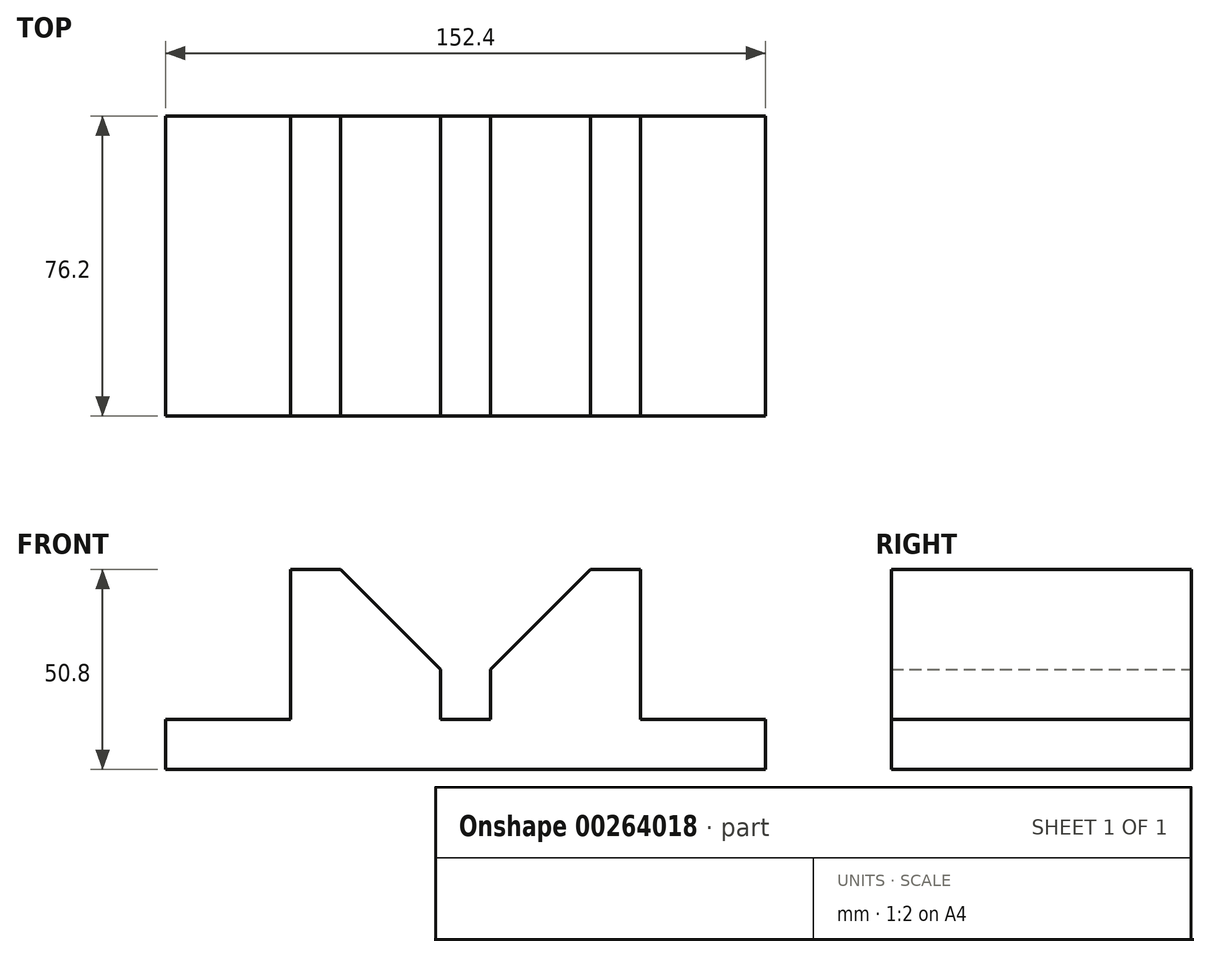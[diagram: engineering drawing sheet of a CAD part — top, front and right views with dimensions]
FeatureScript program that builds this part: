
annotation { "Feature Type Name" : "Feature", "Feature Type Description" : "" }
export const myFeature = defineFeature(function(context is Context, id is Id, definition is map)
    precondition{}
    {
        {
            var Q0;
            Q0=qCreatedBy(makeId("Front.planeOp"),FACE);
            var sketch = newSketch(context, id + "F0", { "sketchPlane" : qUnion([Q0])});
            skLineSegment(sketch, "E0", {"start": v(-76.2, 0) * mm, "end": v(76.2, 0) * mm});
            skLineSegment(sketch, "E1", {"start": v(76.2, 0) * mm, "end": v(76.2, 12.7) * mm});
            skLineSegment(sketch, "E2", {"start": v(76.2, 12.7) * mm, "end": v(44.45, 12.7) * mm});
            skLineSegment(sketch, "E3", {"start": v(44.45, 12.7) * mm, "end": v(44.45, 50.8) * mm});
            skLineSegment(sketch, "E4", {"start": v(44.45, 50.8) * mm, "end": v(31.75, 50.8) * mm});
            skLineSegment(sketch, "E5", {"start": v(-76.2, 0) * mm, "end": v(-76.2, 12.7) * mm});
            skLineSegment(sketch, "E6", {"start": v(-76.2, 12.7) * mm, "end": v(-44.45, 12.7) * mm});
            skLineSegment(sketch, "E7", {"start": v(-44.45, 12.7) * mm, "end": v(-44.45, 50.8) * mm});
            skLineSegment(sketch, "E8", {"start": v(-44.45, 50.8) * mm, "end": v(-31.75, 50.8) * mm});
            skLineSegment(sketch, "E9", {"start": v(6.35, 12.7) * mm, "end": v(6.35, 25.4) * mm});
            skLineSegment(sketch, "E10", {"start": v(6.35, 25.4) * mm, "end": v(31.75, 50.8) * mm});
            skLineSegment(sketch, "E11", {"start": v(6.35, 12.7) * mm, "end": v(-6.35, 12.7) * mm});
            skLineSegment(sketch, "E12", {"start": v(-6.35, 12.7) * mm, "end": v(-6.35, 25.4) * mm});
            skLineSegment(sketch, "E13", {"start": v(-6.35, 25.4) * mm, "end": v(-31.75, 50.8) * mm});
            skSolve(sketch);
        }
        {
            var Q0;
            Q0=makeQuery(id+"F0.imprint","IMPRINT",FACE,{"disambiguationData":[TD([[makeQuery(id+"F0.imprint","IMPRINT",EDGE,{"derivedFrom":sQuery(id+"F0.wireOp",EDGE,"E0")}),1.0]])]});
            extrude(context, id + "F1", {"entities" : qUnion([Q0]), "depth" : 38.1 * mm});
        }
        {
            var Q0;
            Q0=makeQuery(id+"F1.opExtrude","CAP_FACE",FACE,{"disambiguationData":[OSD([sQuery(id+"F0.wireOp",EDGE,"E0"),sQuery(id+"F0.wireOp",EDGE,"E1"),sQuery(id+"F0.wireOp",EDGE,"E2"),sQuery(id+"F0.wireOp",EDGE,"E3"),sQuery(id+"F0.wireOp",EDGE,"E4"),sQuery(id+"F0.wireOp",EDGE,"E5"),sQuery(id+"F0.wireOp",EDGE,"E6"),sQuery(id+"F0.wireOp",EDGE,"E7"),sQuery(id+"F0.wireOp",EDGE,"E8"),sQuery(id+"F0.wireOp",EDGE,"E9"),sQuery(id+"F0.wireOp",EDGE,"E10"),sQuery(id+"F0.wireOp",EDGE,"E11"),sQuery(id+"F0.wireOp",EDGE,"E12"),sQuery(id+"F0.wireOp",EDGE,"E13")])],"isStart":true});
            extrude(context, id + "F2", {"entities" : qUnion([Q0]), "operationType" : NewBodyOperationType.ADD, "depth" : 38.1 * mm});
        }
    });
